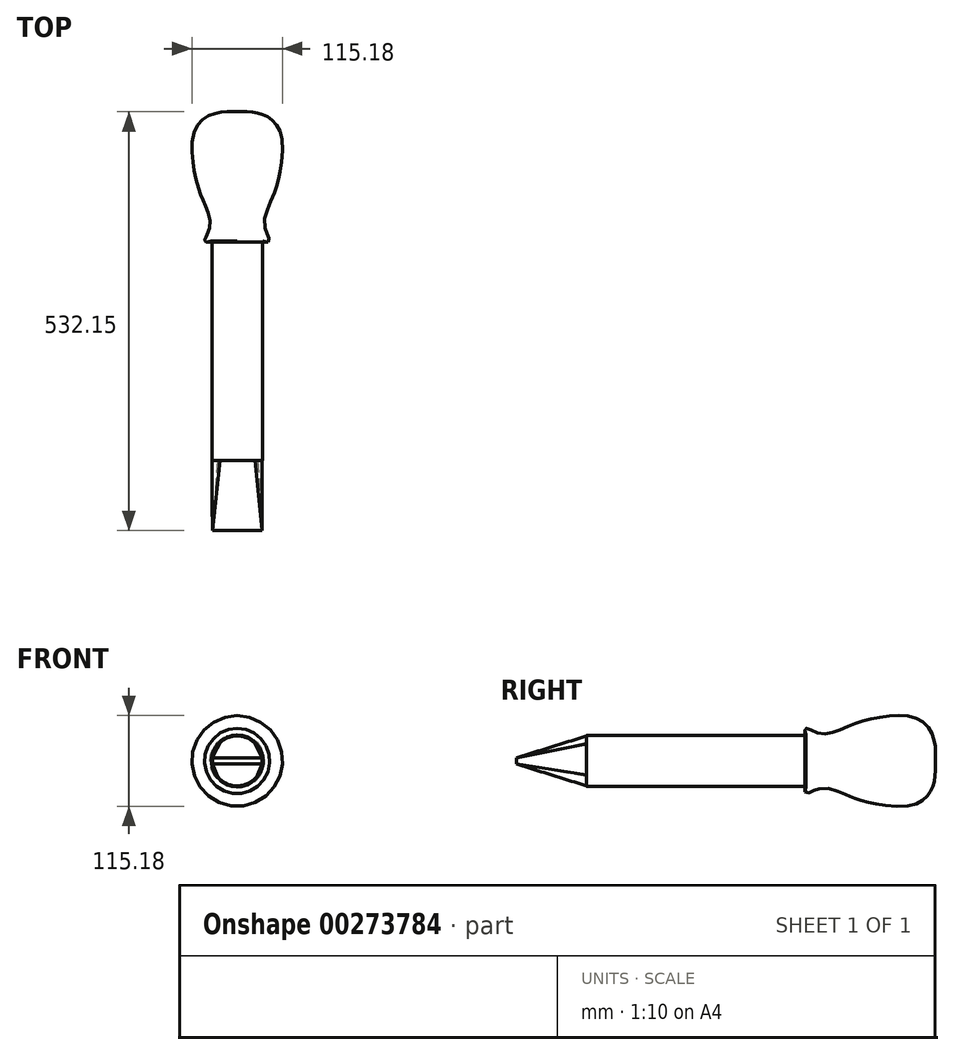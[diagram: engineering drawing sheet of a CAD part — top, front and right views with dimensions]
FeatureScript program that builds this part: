
annotation { "Feature Type Name" : "Feature", "Feature Type Description" : "" }
export const myFeature = defineFeature(function(context is Context, id is Id, definition is map)
    precondition{}
    {
        {
            var Q0;
            Q0=qCreatedBy(makeId("Front.planeOp"),FACE);
            var sketch = newSketch(context, id + "F0", { "sketchPlane" : qUnion([Q0])});
            skArc(sketch, "E0", {"start": v(-22.04, 22.86) * mm, "mid": v(-31.68, 2.08) * mm, "end": v(-24.84, -19.78) * mm});
            skArc(sketch, "E1", {"start": v(23, 21.88) * mm, "mid": v(0.7, 31.74) * mm, "end": v(-22.04, 22.86) * mm});
            skArc(sketch, "E2", {"start": v(26.14, -18.02) * mm, "mid": v(31.65, 2.49) * mm, "end": v(23, 21.88) * mm});
            skArc(sketch, "E3", {"start": v(-24.84, -19.78) * mm, "mid": v(1.1, -31.73) * mm, "end": v(26.14, -18.02) * mm});
            skSolve(sketch);
        }
        {
            var Q0;
            Q0=qCreatedBy(makeId("Front.planeOp"),FACE);
            cPlane(context, id + "F1", {"entities" : qUnion([Q0]), "cplaneType" : CPlaneType.OFFSET, "offset" : 88.9 * mm, "width" : 152.4 * mm, "height" : 152.4 * mm});
        }
        {
            var Q0;
            Q0=qCreatedBy(id+"F1.planeOp",FACE);
            var sketch = newSketch(context, id + "F2", { "sketchPlane" : qUnion([Q0])});
            skLineSegment(sketch, "E4.bottom", {"start": v(-31.58, 4) * mm, "end": v(31.58, 4) * mm});
            skLineSegment(sketch, "E4.top", {"start": v(-31.58, -4) * mm, "end": v(31.58, -4) * mm});
            skLineSegment(sketch, "E4.left", {"start": v(-31.58, 4) * mm, "end": v(-31.58, -4) * mm});
            skLineSegment(sketch, "E4.right", {"start": v(31.58, 4) * mm, "end": v(31.58, -4) * mm});
            skPoint(sketch, "E4.middle", {"position": v(0, 0) * mm});
            skSolve(sketch);
        }
        {
            var Q0;
            Q0=makeQuery(id+"F0.imprint","IMPRINT",FACE,{"disambiguationData":[TD([[makeQuery(id+"F0.imprint","IMPRINT",EDGE,{"derivedFrom":sQuery(id+"F0.wireOp",EDGE,"E0")}),1.0]])]});
            var Q1;
            Q1=makeQuery(id+"F2.imprint","IMPRINT",FACE,{"disambiguationData":[TD([[makeQuery(id+"F2.imprint","IMPRINT",EDGE,{"derivedFrom":sQuery(id+"F2.wireOp",EDGE,"E4.bottom")}),-1.0]])]});
            loft(context, id + "F3", {"sheetProfilesArray" : [{ "sheetProfileEntities" : qUnion([Q0]) }, { "sheetProfileEntities" : qUnion([Q1]) }]});
        }
        {
            var Q0;
            Q0=qCreatedBy(makeId("Front.planeOp"),FACE);
            cPlane(context, id + "F4", {"entities" : qUnion([Q0]), "cplaneType" : CPlaneType.OFFSET, "offset" : 0 * mm, "oppositeDirection" : true, "width" : 152.4 * mm, "height" : 152.4 * mm});
        }
        {
            var Q0;
            Q0=qCreatedBy(id+"F4.planeOp",FACE);
            var sketch = newSketch(context, id + "F5", { "sketchPlane" : qUnion([Q0])});
            skCircle(sketch, "E5", {"center": v(0, 0) * mm, "radius": 32.22 * mm});
            skSolve(sketch);
        }
        {
            var Q0;
            Q0 = qSketchRegion(id + "F5", true);
            extrude(context, id + "F6", {"entities" : qUnion([Q0]), "operationType" : NewBodyOperationType.ADD, "oppositeDirection" : true, "depth" : 279.4 * mm});
        }
        {
            var Q0;
            Q0=qCreatedBy(makeId("Right.planeOp"),FACE);
            var sketch = newSketch(context, id + "F7", { "sketchPlane" : qUnion([Q0])});
            skFitSpline(sketch, "E6", {"points": [v(278.84, 32.78) * mm, v(278.34, 41.2) * mm, v(297.65, 34.76) * mm, v(332.3, 44.16) * mm, v(370.92, 55.06) * mm, v(419.43, 54.07) * mm, v(439.73, 32.28) * mm, v(443.2, 10) * mm, v(443.2, 0) * mm], "startDerivative": vector(-41.4, 158.36) * mm, "endDerivative": vector(-1.66, -113.78) * mm});
            skLineSegment(sketch, "E7", {"start": v(278.84, 32.78) * mm, "end": v(278.84, 0) * mm});
            skLineSegment(sketch, "E8", {"start": v(278.84, 0) * mm, "end": v(443.2, 0) * mm});
            skLineSegment(sketch, "E9", {"start": v(278.84, 0) * mm, "end": v(443.2, 0) * mm, "construction": true});
            skSolve(sketch);
        }
        {
            var Q0;
            Q0=makeQuery(id+"F7.imprint","IMPRINT",FACE,{"disambiguationData":[TD([[makeQuery(id+"F7.imprint","IMPRINT",EDGE,{"derivedFrom":sQuery(id+"F7.wireOp",EDGE,"E6")}),-1.0]])]});
            var Q1;
            Q1=sQuery(id+"F7.wireOp",EDGE,"E8");
            revolve(context, id + "F8", {"operationType" : NewBodyOperationType.ADD, "entities" : qUnion([Q0]), "axis" : qUnion([Q1]), "revolveType" : RevolveType.FULL});
        }
    });
